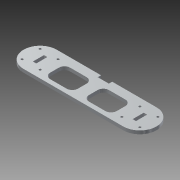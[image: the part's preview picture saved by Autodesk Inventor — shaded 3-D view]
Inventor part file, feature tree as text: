
AUTODESK INVENTOR PART (.ipt)
format: ipt  version: 2015 (Build 190159000, 159)  size: 171,008 bytes
history: native  units: mm
features: extrude x1, sketch x1
ambient origin geometry x8: Origin, YZ Plane, XZ Plane, XY Plane, X Axis, Y Axis, Z Axis, Center Point
bodies: Body1 (feature_tree)
feature tree (2):
  extrude  "Extrusion4"  Depth=15.0mm
  sketch  "Sketch1"  dims[d0=30.0mm d1=120.0mm d2=10.0mm d3=3.0mm d4=13.5mm d5=10.0mm d6=87.0mm d7=3.0mm d8=10.0mm d9=10.0mm d10=15.0mm d11=10.0mm d12=55.0mm d13=3.0mm d16=5.0mm d17=5.0mm d18=30.0mm d19=30.0mm d20=5.0mm d23=25.0mm d24=25.0mm d25=5.0mm d27=8.0mm d30=2.0mm d31=8.132mm d32=8.132mm d33=40.0mm d35=360.0deg d37=2.0mm d40=8.132mm d41=8.132mm d42=40.0mm d44=360.0deg d46=3.0mm d47=0.0mm d48=18.0mm d50=3.0mm d51=15.0mm]
